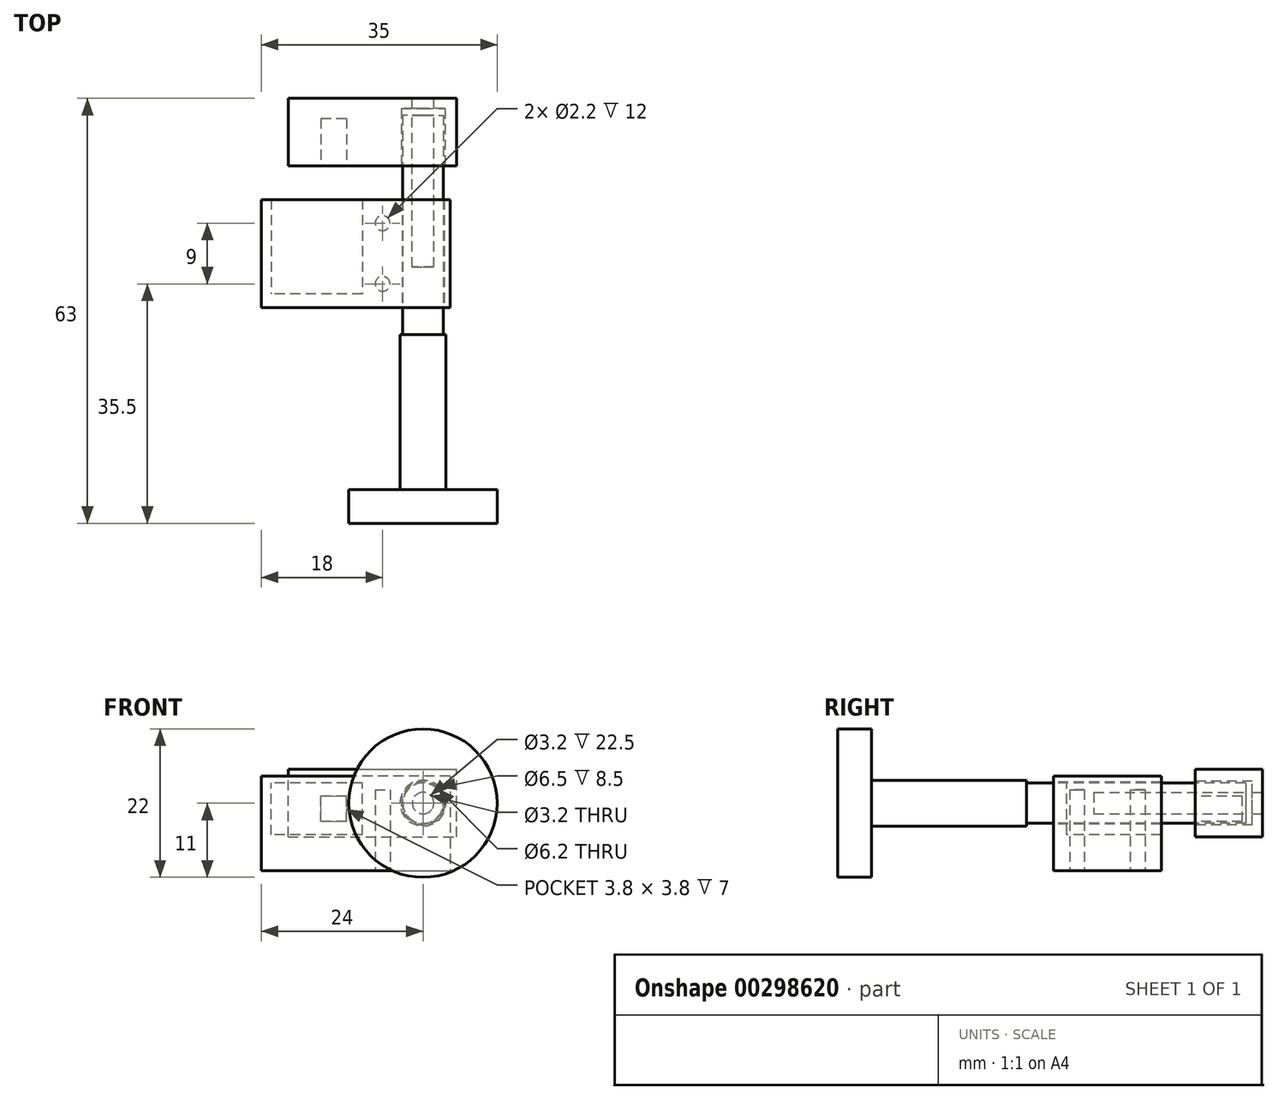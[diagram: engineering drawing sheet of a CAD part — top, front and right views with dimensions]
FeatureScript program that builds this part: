
annotation { "Feature Type Name" : "Feature", "Feature Type Description" : "" }
export const myFeature = defineFeature(function(context is Context, id is Id, definition is map)
    precondition{}
    {
        {
            var Q0;
            Q0=qCreatedBy(makeId("Front.planeOp"),FACE);
            var sketch = newSketch(context, id + "F0", { "sketchPlane" : qUnion([Q0])});
            skLineSegment(sketch, "E0.bottom", {"start": v(-22, -4.85) * mm, "end": v(-50, -4.85) * mm});
            skLineSegment(sketch, "E0.top", {"start": v(-22, 4.85) * mm, "end": v(-50, 4.85) * mm});
            skLineSegment(sketch, "E0.left", {"start": v(-22, -4.85) * mm, "end": v(-22, 4.85) * mm});
            skLineSegment(sketch, "E0.right", {"start": v(-50, -4.85) * mm, "end": v(-50, 4.85) * mm});
            skPoint(sketch, "E0.middle", {"position": v(-36, 0) * mm});
            skLineSegment(sketch, "E1.bottom", {"start": v(-35, -3.85) * mm, "end": v(-48.5, -3.85) * mm});
            skLineSegment(sketch, "E1.top", {"start": v(-35, 3.85) * mm, "end": v(-48.5, 3.85) * mm});
            skLineSegment(sketch, "E1.left", {"start": v(-35, -3.85) * mm, "end": v(-35, 3.85) * mm});
            skLineSegment(sketch, "E1.right", {"start": v(-48.5, -3.85) * mm, "end": v(-48.5, 3.85) * mm});
            skPoint(sketch, "E1.middle", {"position": v(-41.75, 0) * mm});
            skLineSegment(sketch, "E2.bottom", {"start": v(-50, -4.85) * mm, "end": v(-22, -4.85) * mm});
            skLineSegment(sketch, "E2.top", {"start": v(-50, -9.15) * mm, "end": v(-22, -9.15) * mm});
            skLineSegment(sketch, "E2.left", {"start": v(-50, -4.85) * mm, "end": v(-50, -9.15) * mm});
            skLineSegment(sketch, "E2.right", {"start": v(-22, -4.85) * mm, "end": v(-22, -9.15) * mm});
            skCircle(sketch, "E3", {"center": v(-26, 0.85) * mm, "radius": 3.1 * mm});
            skSolve(sketch);
        }
        {
            var Q0;
            Q0=qSketchRegion(id+"F0",true);
            extrude(context, id + "F1", {"entities" : qUnion([Q0]), "oppositeDirection" : true, "depth" : 16 * mm});
        }
        {
            var Q0;
            Q0=makeQuery(id+"F1.opExtrude","CAP_FACE",FACE,{"disambiguationData":[OSD([sQuery(id+"F0.wireOp",EDGE,"E0.bottom"),sQuery(id+"F0.wireOp",EDGE,"E0.top"),sQuery(id+"F0.wireOp",EDGE,"E0.left"),sQuery(id+"F0.wireOp",EDGE,"E0.right"),sQuery(id+"F0.wireOp",EDGE,"E1.bottom"),sQuery(id+"F0.wireOp",EDGE,"E1.top"),sQuery(id+"F0.wireOp",EDGE,"E1.left"),sQuery(id+"F0.wireOp",EDGE,"E1.right"),sQuery(id+"F0.wireOp",EDGE,"IlVQ0T6Q-kpas-WKJO-rE1o-QIE4vgIgB8Sl")])],"isStart":true});
            var sketch = newSketch(context, id + "F2", { "sketchPlane" : qUnion([Q0])});
            skLineSegment(sketch, "E4.bottom", {"start": v(-48.5, 3.85) * mm, "end": v(-35, 3.85) * mm});
            skLineSegment(sketch, "E4.top", {"start": v(-48.5, -3.85) * mm, "end": v(-35, -3.85) * mm});
            skLineSegment(sketch, "E4.left", {"start": v(-35, 3.85) * mm, "end": v(-35, -3.85) * mm});
            skLineSegment(sketch, "E4.right", {"start": v(-48.5, 3.85) * mm, "end": v(-48.5, -3.85) * mm});
            skSolve(sketch);
        }
        {
            var Q0;
            Q0=qSketchRegion(id+"F2",true);
            extrude(context, id + "F3", {"entities" : qUnion([Q0]), "operationType" : NewBodyOperationType.ADD, "oppositeDirection" : true, "depth" : 2 * mm});
        }
        {
            var Q0;
            Q0=makeQuery(id+"F1.opExtrude","SWEPT_FACE",FACE,{"disambiguationData":[OSD([sQuery(id+"F0.wireOp",EDGE,"E2.top")])]});
            var sketch = newSketch(context, id + "F4", { "sketchPlane" : qUnion([Q0])});
            skCircle(sketch, "E5", {"center": v(-32, -3.5) * mm, "radius": 1.1 * mm});
            skCircle(sketch, "E6", {"center": v(-32, -12.5) * mm, "radius": 1.1 * mm});
            skSolve(sketch);
        }
        {
            var Q0;
            Q0=qSketchRegion(id+"F4",true);
            extrude(context, id + "F5", {"entities" : qUnion([Q0]), "operationType" : NewBodyOperationType.REMOVE, "oppositeDirection" : true, "depth" : 12 * mm});
        }
        {
            var Q0;
            Q0=makeQuery(id+"F1.opExtrude","CAP_FACE",FACE,{"disambiguationData":[OSD([sQuery(id+"F0.wireOp",EDGE,"E0.top"),sQuery(id+"F0.wireOp",EDGE,"E0.left"),sQuery(id+"F0.wireOp",EDGE,"E0.right"),sQuery(id+"F0.wireOp",EDGE,"E1.bottom"),sQuery(id+"F0.wireOp",EDGE,"E1.top"),sQuery(id+"F0.wireOp",EDGE,"E1.left"),sQuery(id+"F0.wireOp",EDGE,"E1.right"),sQuery(id+"F0.wireOp",EDGE,"E2.top"),sQuery(id+"F0.wireOp",EDGE,"E2.left"),sQuery(id+"F0.wireOp",EDGE,"E2.right"),sQuery(id+"F0.wireOp",EDGE,"E3")])],"isStart":false});
            cPlane(context, id + "F6", {"entities" : qUnion([Q0]), "cplaneType" : CPlaneType.OFFSET, "offset" : 5 * mm, "width" : 150 * mm, "height" : 150 * mm});
        }
        {
            var Q0;
            Q0=qCreatedBy(makeId("Front.planeOp"),FACE);
            cPlane(context, id + "F7", {"entities" : qUnion([Q0]), "cplaneType" : CPlaneType.OFFSET, "offset" : 27 * mm, "width" : 150 * mm, "height" : 150 * mm});
        }
        {
            var Q0;
            Q0=qCreatedBy(id+"F7.planeOp",FACE);
            var sketch = newSketch(context, id + "F8", { "sketchPlane" : qUnion([Q0])});
            skCircle(sketch, "E7", {"center": v(-26, 0.85) * mm, "radius": 11 * mm});
            skSolve(sketch);
        }
        {
            var Q0;
            Q0=qSketchRegion(id+"F8",true);
            extrude(context, id + "F9", {"entities" : qUnion([Q0]), "depth" : 5 * mm});
        }
        {
            var Q0;
            Q0=makeQuery(id+"F9.opExtrude","CAP_FACE",FACE,{"disambiguationData":[OSD([sQuery(id+"F8.wireOp",EDGE,"E7")])],"isStart":true});
            var sketch = newSketch(context, id + "F10", { "sketchPlane" : qUnion([Q0])});
            skCircle(sketch, "E8", {"center": v(26, 0.85) * mm, "radius": 3 * mm});
            skSolve(sketch);
        }
        {
            var Q0;
            Q0=qSketchRegion(id+"F10",true);
            extrude(context, id + "F11", {"entities" : qUnion([Q0]), "operationType" : NewBodyOperationType.ADD, "depth" : 48 * mm});
        }
        {
            var Q0;
            Q0=qCreatedBy(id+"F6.planeOp",FACE);
            var sketch = newSketch(context, id + "F12", { "sketchPlane" : qUnion([Q0])});
            skLineSegment(sketch, "E9.bottom", {"start": v(46, -4.15) * mm, "end": v(21, -4.15) * mm});
            skLineSegment(sketch, "E9.top", {"start": v(46, 5.85) * mm, "end": v(21, 5.85) * mm});
            skLineSegment(sketch, "E9.left", {"start": v(46, -4.15) * mm, "end": v(46, 5.85) * mm});
            skLineSegment(sketch, "E9.right", {"start": v(21, -4.15) * mm, "end": v(21, 5.85) * mm});
            skSolve(sketch);
        }
        {
            var Q0;
            Q0=qSketchRegion(id+"F12",true);
            extrude(context, id + "F13", {"entities" : qUnion([Q0]), "depth" : 10 * mm});
        }
        {
            var Q0;
            Q0=makeQuery(id+"F13.opExtrude","CAP_FACE",FACE,{"disambiguationData":[OSD([sQuery(id+"F12.wireOp",EDGE,"E9.bottom"),sQuery(id+"F12.wireOp",EDGE,"E9.top"),sQuery(id+"F12.wireOp",EDGE,"E9.left"),sQuery(id+"F12.wireOp",EDGE,"E9.right")])],"isStart":true});
            var sketch = newSketch(context, id + "F14", { "sketchPlane" : qUnion([Q0])});
            skLineSegment(sketch, "E10.bottom", {"start": v(-37.35, -1.9) * mm, "end": v(-41.15, -1.9) * mm});
            skLineSegment(sketch, "E10.top", {"start": v(-37.35, 1.9) * mm, "end": v(-41.15, 1.9) * mm});
            skLineSegment(sketch, "E10.left", {"start": v(-37.35, -1.9) * mm, "end": v(-37.35, 1.9) * mm});
            skLineSegment(sketch, "E10.right", {"start": v(-41.15, -1.9) * mm, "end": v(-41.15, 1.9) * mm});
            skPoint(sketch, "E10.middle", {"position": v(-39.25, 0) * mm});
            skCircle(sketch, "E11", {"center": v(-26, 0.85) * mm, "radius": 3.25 * mm});
            skSolve(sketch);
        }
        {
            var Q0;
            Q0=makeQuery(id+"F14.imprint","IMPRINT",FACE,{"disambiguationData":[TD([[makeQuery(id+"F14.imprint","IMPRINT",EDGE,{"derivedFrom":sQuery(id+"F14.wireOp",EDGE,"E10.bottom")}),-1.0]])]});
            extrude(context, id + "F15", {"entities" : qUnion([Q0]), "operationType" : NewBodyOperationType.REMOVE, "oppositeDirection" : true, "depth" : 7 * mm});
        }
        {
            var Q0;
            Q0=makeQuery(id+"F14.imprint","IMPRINT",FACE,{"disambiguationData":[TD([[makeQuery(id+"F14.imprint","IMPRINT",EDGE,{"derivedFrom":sQuery(id+"F14.wireOp",EDGE,"E11")}),1.0]])]});
            extrude(context, id + "F16", {"entities" : qUnion([Q0]), "operationType" : NewBodyOperationType.REMOVE, "oppositeDirection" : true, "depth" : 8.5 * mm});
        }
        {
            var Q0;
            Q0=makeQuery(id+"F8.imprint","IMPRINT",FACE,{"disambiguationData":[TD([[makeQuery(id+"F8.imprint","IMPRINT",EDGE,{"derivedFrom":sQuery(id+"F8.wireOp",EDGE,"E7")}),1.0]])]});
            var sketch = newSketch(context, id + "F17", { "sketchPlane" : qUnion([Q0])});
            skCircle(sketch, "E12", {"center": v(-26, 0.85) * mm, "radius": 3.4 * mm});
            skSolve(sketch);
        }
        {
            var Q0;
            Q0=qSketchRegion(id+"F17",true);
            extrude(context, id + "F18", {"entities" : qUnion([Q0]), "operationType" : NewBodyOperationType.ADD, "oppositeDirection" : true, "depth" : 23 * mm});
        }
        {
            var Q0;
            Q0=makeQuery(id+"F11.opExtrude","CAP_FACE",FACE,{"disambiguationData":[OSD([sQuery(id+"F10.wireOp",EDGE,"E8")])],"isStart":false});
            var sketch = newSketch(context, id + "F19", { "sketchPlane" : qUnion([Q0])});
            skCircle(sketch, "E13", {"center": v(26, 0.85) * mm, "radius": 3 * mm});
            skSolve(sketch);
        }
        {
            var Q0;
            Q0=qSketchRegion(id+"F19",true);
            extrude(context, id + "F20", {"entities" : qUnion([Q0]), "operationType" : NewBodyOperationType.ADD, "depth" : 7.5 * mm});
        }
        {
            var Q0;
            Q0=makeQuery(id+"F20.opExtrude","CAP_FACE",FACE,{"disambiguationData":[OSD([sQuery(id+"F19.wireOp",EDGE,"E13")])],"isStart":false});
            var sketch = newSketch(context, id + "F21", { "sketchPlane" : qUnion([Q0])});
            skCircle(sketch, "E14", {"center": v(26, 0.85) * mm, "radius": 1.1 * mm});
            skSolve(sketch);
        }
        {
            var Q0;
            Q0=qSketchRegion(id+"F21",true);
            extrude(context, id + "F22", {"entities" : qUnion([Q0]), "operationType" : NewBodyOperationType.REMOVE, "oppositeDirection" : true, "depth" : 12 * mm});
        }
        {
            var Q0;
            Q0=makeQuery(id+"F13.opExtrude","CAP_FACE",FACE,{"disambiguationData":[OSD([sQuery(id+"F12.wireOp",EDGE,"E9.bottom"),sQuery(id+"F12.wireOp",EDGE,"E9.top"),sQuery(id+"F12.wireOp",EDGE,"E9.left"),sQuery(id+"F12.wireOp",EDGE,"E9.right")])],"isStart":false});
            var sketch = newSketch(context, id + "F23", { "sketchPlane" : qUnion([Q0])});
            skCircle(sketch, "E15", {"center": v(26, 0.85) * mm, "radius": 1.6 * mm});
            skSolve(sketch);
        }
        {
            var Q0;
            Q0=qSketchRegion(id+"F23",true);
            extrude(context, id + "F24", {"entities" : qUnion([Q0]), "operationType" : NewBodyOperationType.REMOVE, "oppositeDirection" : true, "depth" : 25 * mm});
        }
    });
